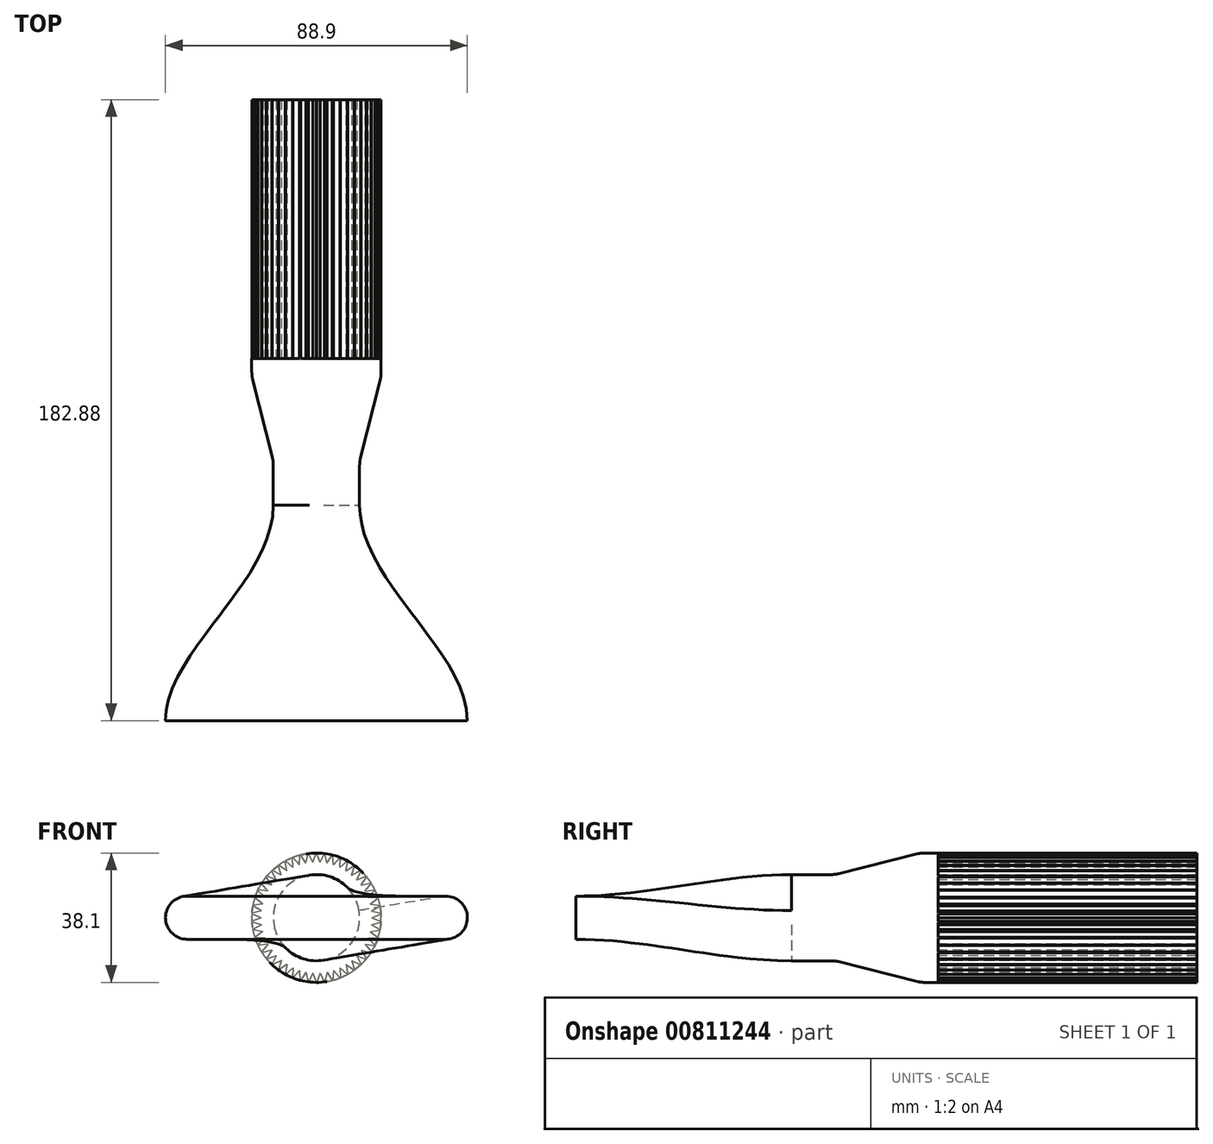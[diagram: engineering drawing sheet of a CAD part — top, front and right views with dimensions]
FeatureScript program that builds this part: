
annotation { "Feature Type Name" : "Feature", "Feature Type Description" : "" }
export const myFeature = defineFeature(function(context is Context, id is Id, definition is map)
    precondition{}
    {
        {
            var Q0;
            Q0=qCreatedBy(makeId("Front.planeOp"),FACE);
            var sketch = newSketch(context, id + "F0", { "sketchPlane" : qUnion([Q0])});
            skLineSegment(sketch, "E0.bottom", {"start": v(38.1, 6.35) * mm, "end": v(-38.1, 6.35) * mm});
            skLineSegment(sketch, "E0.top", {"start": v(38.1, -6.35) * mm, "end": v(-38.1, -6.35) * mm});
            skLineSegment(sketch, "E0.left", {"start": v(38.1, 6.35) * mm, "end": v(38.1, -6.35) * mm});
            skLineSegment(sketch, "E0.right", {"start": v(-38.1, 6.35) * mm, "end": v(-38.1, -6.35) * mm});
            skPoint(sketch, "E0.middle", {"position": v(0, 0) * mm});
            skArc(sketch, "E1", {"start": v(-38.1, 6.35) * mm, "mid": v(-44.45, 0) * mm, "end": v(-38.1, -6.35) * mm});
            skArc(sketch, "E2", {"start": v(38.1, -6.35) * mm, "mid": v(44.45, 0) * mm, "end": v(38.1, 6.35) * mm});
            skSolve(sketch);
        }
        {
            var Q0;
            Q0=qCreatedBy(makeId("Front.planeOp"),FACE);
            cPlane(context, id + "F1", {"entities" : qUnion([Q0]), "cplaneType" : CPlaneType.OFFSET, "offset" : 63.5 * mm, "oppositeDirection" : true, "width" : 152.4 * mm, "height" : 152.4 * mm});
        }
        {
            var Q0;
            Q0=qCreatedBy(id+"F1.planeOp",FACE);
            var sketch = newSketch(context, id + "F2", { "sketchPlane" : qUnion([Q0])});
            skCircle(sketch, "E3", {"center": v(0, 0) * mm, "radius": 12.7 * mm});
            skSolve(sketch);
        }
        {
            var Q0;
            Q0 = qSketchRegion(id + "F0", true);
            var Q1;
            Q1 = qSketchRegion(id + "F2", true);
            loft(context, id + "F3", {"startCondition" : LoftEndDerivativeType.NORMAL_TO_PROFILE, "startMagnitude" : 1, "endCondition" : LoftEndDerivativeType.NORMAL_TO_PROFILE, "endMagnitude" : 1, "sheetProfilesArray" : [{ "sheetProfileEntities" : qUnion([Q0]) }, { "sheetProfileEntities" : qUnion([Q1]) }]});
        }
        {
            var Q0;
            Q0=makeQuery(id+"F3.opLoft","CAP_FACE",FACE,{"disambiguationData":[OSD([makeQuery(id+"F2.imprint","IMPRINT",FACE,{"disambiguationData":[TD([[makeQuery(id+"F2.imprint","IMPRINT",EDGE,{"derivedFrom":sQuery(id+"F2.wireOp",EDGE,"E3")}),1.0]])]})])],"isStart":true});
            extrude(context, id + "F4", {"entities" : qUnion([Q0]), "operationType" : NewBodyOperationType.ADD, "depth" : 12.7 * mm, "offsetDistance" : 25.4 * mm});
        }
        {
            var Q0;
            Q0=makeQuery(id+"F4.opExtrude","CAP_FACE",FACE,{"disambiguationData":[OSD([makeQuery(id+"F2.imprint","IMPRINT",FACE,{"disambiguationData":[TD([[makeQuery(id+"F2.imprint","IMPRINT",EDGE,{"derivedFrom":sQuery(id+"F2.wireOp",EDGE,"E3")}),1.0]])]})])],"isStart":false});
            cPlane(context, id + "F5", {"entities" : qUnion([Q0]), "cplaneType" : CPlaneType.OFFSET, "offset" : 25.4 * mm, "width" : 152.4 * mm, "height" : 152.4 * mm});
        }
        {
            var Q0;
            Q0=qCreatedBy(id+"F5.planeOp",FACE);
            var sketch = newSketch(context, id + "F6", { "sketchPlane" : qUnion([Q0])});
            skCircle(sketch, "E4", {"center": v(0, 0) * mm, "radius": 19.05 * mm});
            skSolve(sketch);
        }
        {
            var Q1;
            Q1=makeQuery(id+"F6.imprint","IMPRINT",FACE,{"disambiguationData":[TD([[makeQuery(id+"F6.imprint","IMPRINT",EDGE,{"derivedFrom":sQuery(id+"F6.wireOp",EDGE,"E4")}),1.0]])]});
            var Q2;
            Q2=makeQuery(id+"F4.opExtrude","CAP_FACE",FACE,{"disambiguationData":[OSD([makeQuery(id+"F2.imprint","IMPRINT",FACE,{"disambiguationData":[TD([[makeQuery(id+"F2.imprint","IMPRINT",EDGE,{"derivedFrom":sQuery(id+"F2.wireOp",EDGE,"E3")}),1.0]])]})])],"isStart":false});
            loft(context, id + "F7", {"operationType" : NewBodyOperationType.ADD, "sheetProfilesArray" : [{ "sheetProfileEntities" : qUnion([Q1]) }, { "sheetProfileEntities" : qUnion([Q2]) }]});
        }
        {
            var Q0;
            Q0=makeQuery(id+"F7.opLoft","CAP_FACE",FACE,{"disambiguationData":[OSD([makeQuery(id+"F6.imprint","IMPRINT",FACE,{"disambiguationData":[TD([[makeQuery(id+"F6.imprint","IMPRINT",EDGE,{"derivedFrom":sQuery(id+"F6.wireOp",EDGE,"E4")}),1.0]])]})])],"isStart":true});
            extrude(context, id + "F8", {"entities" : qUnion([Q0]), "operationType" : NewBodyOperationType.ADD, "depth" : 5.08 * mm, "offsetDistance" : 25.4 * mm});
        }
        {
            var Q0;
            Q0=makeQuery(id+"F8.opExtrude","CAP_FACE",FACE,{"disambiguationData":[OSD([makeQuery(id+"F6.imprint","IMPRINT",FACE,{"disambiguationData":[TD([[makeQuery(id+"F6.imprint","IMPRINT",EDGE,{"derivedFrom":sQuery(id+"F6.wireOp",EDGE,"E4")}),1.0]])]})])],"isStart":false});
            var sketch = newSketch(context, id + "F9", { "sketchPlane" : qUnion([Q0])});
            skLineSegment(sketch, "E5", {"start": v(-16.3, 0) * mm, "end": v(-19.02, 1.1) * mm});
            skLineSegment(sketch, "E6.MirrorCS", {"start": v(-16.3, 0) * mm, "end": v(-19.02, -1.1) * mm});
            skLineSegment(sketch, "E7.1.0", {"start": v(-16.18, -2.04) * mm, "end": v(-19, -1.3) * mm});
            skLineSegment(sketch, "E7.1.1", {"start": v(-16.18, -2.04) * mm, "end": v(-18.73, -3.47) * mm});
            skLineSegment(sketch, "E7.2.0", {"start": v(-15.8, -4.06) * mm, "end": v(-18.7, -3.67) * mm});
            skLineSegment(sketch, "E7.2.1", {"start": v(-15.8, -4.06) * mm, "end": v(-18.15, -5.8) * mm});
            skLineSegment(sketch, "E7.3.0", {"start": v(-15.16, -6) * mm, "end": v(-18.09, -5.98) * mm});
            skLineSegment(sketch, "E7.3.1", {"start": v(-15.16, -6) * mm, "end": v(-17.28, -8.02) * mm});
            skPoint(sketch, "E7.center", {"position": v(0, 0) * mm});
            skLineSegment(sketch, "E8.3.4.0", {"start": v(-14.3, -7.86) * mm, "end": v(-16.14, -10.13) * mm});
            skLineSegment(sketch, "E8.5.4.0", {"start": v(-14.3, -7.86) * mm, "end": v(-17.2, -8.2) * mm});
            skLineSegment(sketch, "E8.3.5.0", {"start": v(-13.2, -9.59) * mm, "end": v(-14.74, -12.07) * mm});
            skLineSegment(sketch, "E8.5.5.0", {"start": v(-13.2, -9.59) * mm, "end": v(-16.03, -10.29) * mm});
            skLineSegment(sketch, "E8.3.6.0", {"start": v(-11.89, -11.16) * mm, "end": v(-13.11, -13.82) * mm});
            skLineSegment(sketch, "E8.5.6.0", {"start": v(-11.89, -11.16) * mm, "end": v(-14.62, -12.22) * mm});
            skLineSegment(sketch, "E8.3.7.0", {"start": v(-10.4, -12.57) * mm, "end": v(-11.28, -15.35) * mm});
            skLineSegment(sketch, "E8.5.7.0", {"start": v(-10.4, -12.57) * mm, "end": v(-12.97, -13.95) * mm});
            skLineSegment(sketch, "E8.3.8.0", {"start": v(-8.74, -13.77) * mm, "end": v(-9.26, -16.65) * mm});
            skLineSegment(sketch, "E8.5.8.0", {"start": v(-8.74, -13.77) * mm, "end": v(-11.12, -15.47) * mm});
            skLineSegment(sketch, "E8.3.9.0", {"start": v(-6.94, -14.76) * mm, "end": v(-7.1, -17.68) * mm});
            skLineSegment(sketch, "E8.5.9.0", {"start": v(-6.94, -14.76) * mm, "end": v(-9.1, -16.74) * mm});
            skLineSegment(sketch, "E8.3.10.0", {"start": v(-5.04, -15.51) * mm, "end": v(-4.83, -18.43) * mm});
            skLineSegment(sketch, "E8.5.10.0", {"start": v(-5.04, -15.51) * mm, "end": v(-6.92, -17.75) * mm});
            skLineSegment(sketch, "E8.3.11.0", {"start": v(-3.06, -16.02) * mm, "end": v(-2.48, -18.89) * mm});
            skLineSegment(sketch, "E8.5.11.0", {"start": v(-3.06, -16.02) * mm, "end": v(-4.64, -18.48) * mm});
            skLineSegment(sketch, "E8.3.12.0", {"start": v(-1.02, -16.28) * mm, "end": v(-0.1, -19.05) * mm});
            skLineSegment(sketch, "E8.5.12.0", {"start": v(-1.02, -16.28) * mm, "end": v(-2.3, -18.91) * mm});
            skLineSegment(sketch, "E8.3.13.0", {"start": v(1.02, -16.28) * mm, "end": v(2.3, -18.91) * mm});
            skLineSegment(sketch, "E8.5.13.0", {"start": v(1.02, -16.28) * mm, "end": v(0.1, -19.05) * mm});
            skLineSegment(sketch, "E8.3.14.0", {"start": v(3.06, -16.02) * mm, "end": v(4.64, -18.48) * mm});
            skLineSegment(sketch, "E8.5.14.0", {"start": v(3.06, -16.02) * mm, "end": v(2.48, -18.89) * mm});
            skLineSegment(sketch, "E8.3.15.0", {"start": v(5.04, -15.51) * mm, "end": v(6.92, -17.75) * mm});
            skLineSegment(sketch, "E8.5.15.0", {"start": v(5.04, -15.51) * mm, "end": v(4.83, -18.43) * mm});
            skLineSegment(sketch, "E8.3.16.0", {"start": v(6.94, -14.76) * mm, "end": v(9.1, -16.74) * mm});
            skLineSegment(sketch, "E8.5.16.0", {"start": v(6.94, -14.76) * mm, "end": v(7.1, -17.68) * mm});
            skLineSegment(sketch, "E8.3.17.0", {"start": v(8.74, -13.77) * mm, "end": v(11.12, -15.47) * mm});
            skLineSegment(sketch, "E8.5.17.0", {"start": v(8.74, -13.77) * mm, "end": v(9.26, -16.65) * mm});
            skLineSegment(sketch, "E8.3.18.0", {"start": v(10.4, -12.57) * mm, "end": v(12.97, -13.95) * mm});
            skLineSegment(sketch, "E8.5.18.0", {"start": v(10.4, -12.57) * mm, "end": v(11.28, -15.35) * mm});
            skLineSegment(sketch, "E8.3.19.0", {"start": v(11.89, -11.16) * mm, "end": v(14.62, -12.22) * mm});
            skLineSegment(sketch, "E8.5.19.0", {"start": v(11.89, -11.16) * mm, "end": v(13.11, -13.82) * mm});
            skLineSegment(sketch, "E8.3.20.0", {"start": v(13.2, -9.59) * mm, "end": v(16.03, -10.29) * mm});
            skLineSegment(sketch, "E8.5.20.0", {"start": v(13.2, -9.59) * mm, "end": v(14.74, -12.07) * mm});
            skLineSegment(sketch, "E8.3.21.0", {"start": v(14.3, -7.86) * mm, "end": v(17.2, -8.2) * mm});
            skLineSegment(sketch, "E8.5.21.0", {"start": v(14.3, -7.86) * mm, "end": v(16.14, -10.13) * mm});
            skLineSegment(sketch, "E8.3.22.0", {"start": v(15.16, -6) * mm, "end": v(18.09, -5.98) * mm});
            skLineSegment(sketch, "E8.5.22.0", {"start": v(15.16, -6) * mm, "end": v(17.28, -8.02) * mm});
            skLineSegment(sketch, "E8.3.23.0", {"start": v(15.8, -4.06) * mm, "end": v(18.7, -3.67) * mm});
            skLineSegment(sketch, "E8.5.23.0", {"start": v(15.8, -4.06) * mm, "end": v(18.15, -5.8) * mm});
            skLineSegment(sketch, "E8.3.24.0", {"start": v(16.18, -2.04) * mm, "end": v(19, -1.3) * mm});
            skLineSegment(sketch, "E8.5.24.0", {"start": v(16.18, -2.04) * mm, "end": v(18.73, -3.47) * mm});
            skLineSegment(sketch, "E8.3.25.0", {"start": v(16.3, 0) * mm, "end": v(19.02, 1.1) * mm});
            skLineSegment(sketch, "E8.5.25.0", {"start": v(16.3, 0) * mm, "end": v(19.02, -1.1) * mm});
            skLineSegment(sketch, "E8.3.26.0", {"start": v(16.18, 2.04) * mm, "end": v(18.73, 3.47) * mm});
            skLineSegment(sketch, "E8.5.26.0", {"start": v(16.18, 2.04) * mm, "end": v(19, 1.3) * mm});
            skLineSegment(sketch, "E8.3.27.0", {"start": v(15.8, 4.06) * mm, "end": v(18.15, 5.8) * mm});
            skLineSegment(sketch, "E8.5.27.0", {"start": v(15.8, 4.06) * mm, "end": v(18.7, 3.67) * mm});
            skLineSegment(sketch, "E8.3.28.0", {"start": v(15.16, 6) * mm, "end": v(17.28, 8.02) * mm});
            skLineSegment(sketch, "E8.5.28.0", {"start": v(15.16, 6) * mm, "end": v(18.09, 5.98) * mm});
            skLineSegment(sketch, "E8.3.29.0", {"start": v(14.3, 7.86) * mm, "end": v(16.14, 10.13) * mm});
            skLineSegment(sketch, "E8.5.29.0", {"start": v(14.3, 7.86) * mm, "end": v(17.2, 8.2) * mm});
            skLineSegment(sketch, "E8.3.30.0", {"start": v(13.2, 9.59) * mm, "end": v(14.74, 12.07) * mm});
            skLineSegment(sketch, "E8.5.30.0", {"start": v(13.2, 9.59) * mm, "end": v(16.03, 10.29) * mm});
            skLineSegment(sketch, "E8.3.31.0", {"start": v(11.89, 11.16) * mm, "end": v(13.11, 13.82) * mm});
            skLineSegment(sketch, "E8.5.31.0", {"start": v(11.89, 11.16) * mm, "end": v(14.62, 12.22) * mm});
            skLineSegment(sketch, "E8.3.32.0", {"start": v(10.4, 12.57) * mm, "end": v(11.28, 15.35) * mm});
            skLineSegment(sketch, "E8.5.32.0", {"start": v(10.4, 12.57) * mm, "end": v(12.97, 13.95) * mm});
            skLineSegment(sketch, "E8.3.33.0", {"start": v(8.74, 13.77) * mm, "end": v(9.26, 16.65) * mm});
            skLineSegment(sketch, "E8.5.33.0", {"start": v(8.74, 13.77) * mm, "end": v(11.12, 15.47) * mm});
            skLineSegment(sketch, "E8.3.34.0", {"start": v(6.94, 14.76) * mm, "end": v(7.1, 17.68) * mm});
            skLineSegment(sketch, "E8.5.34.0", {"start": v(6.94, 14.76) * mm, "end": v(9.1, 16.74) * mm});
            skLineSegment(sketch, "E8.3.35.0", {"start": v(5.04, 15.51) * mm, "end": v(4.83, 18.43) * mm});
            skLineSegment(sketch, "E8.5.35.0", {"start": v(5.04, 15.51) * mm, "end": v(6.92, 17.75) * mm});
            skLineSegment(sketch, "E8.3.36.0", {"start": v(3.06, 16.02) * mm, "end": v(2.48, 18.89) * mm});
            skLineSegment(sketch, "E8.5.36.0", {"start": v(3.06, 16.02) * mm, "end": v(4.64, 18.48) * mm});
            skLineSegment(sketch, "E8.3.37.0", {"start": v(1.02, 16.28) * mm, "end": v(0.1, 19.05) * mm});
            skLineSegment(sketch, "E8.5.37.0", {"start": v(1.02, 16.28) * mm, "end": v(2.3, 18.91) * mm});
            skLineSegment(sketch, "E8.3.38.0", {"start": v(-1.02, 16.28) * mm, "end": v(-2.3, 18.91) * mm});
            skLineSegment(sketch, "E8.5.38.0", {"start": v(-1.02, 16.28) * mm, "end": v(-0.1, 19.05) * mm});
            skLineSegment(sketch, "E8.3.39.0", {"start": v(-3.06, 16.02) * mm, "end": v(-4.64, 18.48) * mm});
            skLineSegment(sketch, "E8.5.39.0", {"start": v(-3.06, 16.02) * mm, "end": v(-2.48, 18.89) * mm});
            skLineSegment(sketch, "E8.3.40.0", {"start": v(-5.04, 15.51) * mm, "end": v(-6.92, 17.75) * mm});
            skLineSegment(sketch, "E8.5.40.0", {"start": v(-5.04, 15.51) * mm, "end": v(-4.83, 18.43) * mm});
            skLineSegment(sketch, "E8.3.41.0", {"start": v(-6.94, 14.76) * mm, "end": v(-9.1, 16.74) * mm});
            skLineSegment(sketch, "E8.5.41.0", {"start": v(-6.94, 14.76) * mm, "end": v(-7.1, 17.68) * mm});
            skLineSegment(sketch, "E8.3.42.0", {"start": v(-8.74, 13.77) * mm, "end": v(-11.12, 15.47) * mm});
            skLineSegment(sketch, "E8.5.42.0", {"start": v(-8.74, 13.77) * mm, "end": v(-9.26, 16.65) * mm});
            skLineSegment(sketch, "E8.3.43.0", {"start": v(-10.4, 12.57) * mm, "end": v(-12.97, 13.95) * mm});
            skLineSegment(sketch, "E8.5.43.0", {"start": v(-10.4, 12.57) * mm, "end": v(-11.28, 15.35) * mm});
            skLineSegment(sketch, "E8.3.44.0", {"start": v(-11.89, 11.16) * mm, "end": v(-14.62, 12.22) * mm});
            skLineSegment(sketch, "E8.5.44.0", {"start": v(-11.89, 11.16) * mm, "end": v(-13.11, 13.82) * mm});
            skLineSegment(sketch, "E8.3.45.0", {"start": v(-13.2, 9.59) * mm, "end": v(-16.03, 10.29) * mm});
            skLineSegment(sketch, "E8.5.45.0", {"start": v(-13.2, 9.59) * mm, "end": v(-14.74, 12.07) * mm});
            skLineSegment(sketch, "E8.3.46.0", {"start": v(-14.3, 7.86) * mm, "end": v(-17.2, 8.2) * mm});
            skLineSegment(sketch, "E8.5.46.0", {"start": v(-14.3, 7.86) * mm, "end": v(-16.14, 10.13) * mm});
            skLineSegment(sketch, "E8.3.47.0", {"start": v(-15.16, 6) * mm, "end": v(-18.09, 5.98) * mm});
            skLineSegment(sketch, "E8.5.47.0", {"start": v(-15.16, 6) * mm, "end": v(-17.28, 8.02) * mm});
            skLineSegment(sketch, "E8.3.48.0", {"start": v(-15.8, 4.06) * mm, "end": v(-18.7, 3.67) * mm});
            skLineSegment(sketch, "E8.5.48.0", {"start": v(-15.8, 4.06) * mm, "end": v(-18.15, 5.8) * mm});
            skLineSegment(sketch, "E8.3.49.0", {"start": v(-16.18, 2.04) * mm, "end": v(-19, 1.3) * mm});
            skLineSegment(sketch, "E8.5.49.0", {"start": v(-16.18, 2.04) * mm, "end": v(-18.73, 3.47) * mm});
            skSolve(sketch);
        }
        {
            var Q0;
            {var subQ77=sQuery(id+"F9.wireOp",EDGE,"E5");Q0=makeQuery(id+"F9.imprint","IMPRINT",FACE,{"disambiguationData":[TD([[makeQuery(id+"F9.imprint","IMPRINT",EDGE,{"derivedFrom":subQ77}),-1.0]])]});}
            extrude(context, id + "F10", {"entities" : qUnion([Q0]), "operationType" : NewBodyOperationType.ADD, "depth" : 76.2 * mm, "offsetDistance" : 25.4 * mm});
        }
        {
            var Q0;
            {var subQ0=sQuery(id+"F6.wireOp",EDGE,"E4");var subQ1=sQuery(id+"F2.wireOp",EDGE,"E3");var subQ2=sQuery(id+"F0.wireOp",EDGE,"E1");var subQ3=sQuery(id+"F0.wireOp",EDGE,"E0.right");var subQ4=sQuery(id+"F0.wireOp",EDGE,"E0.top");var subQ5=sQuery(id+"F0.wireOp",EDGE,"E2");var subQ6=sQuery(id+"F0.wireOp",EDGE,"E0.left");var subQ7=sQuery(id+"F0.wireOp",EDGE,"E0.bottom");var subQ8=makeQuery(id+"F7.opLoft","MID_CAP_EDGE",EDGE,{"disambiguationData":[OSD([subQ7,subQ4,subQ6,subQ3,subQ2,subQ5,subQ1,subQ0]),TDD([makeQuery(id+"F4.opExtrude","CAP_VERTEX",VERTEX,{"disambiguationData":[OSD([subQ7,subQ6,subQ5,subQ1])],"isStart":false}),makeQuery(id+"F4.opExtrude","CAP_VERTEX",VERTEX,{"disambiguationData":[OSD([subQ4,subQ3,subQ2,subQ1])],"isStart":false}),makeQuery(id+"F6.imprint","IMPRINT",EDGE,{"derivedFrom":subQ0})])],"capPos":0.0});Q0=makeQuery(id+"F8.boolean.opBoolean","MERGE",EDGE,{"derivedFrom":[subQ8,makeQuery(id+"F8.opExtrude","CAP_EDGE",EDGE,{"disambiguationData":[OSD([subQ7,subQ4,subQ6,subQ3,subQ2,subQ5,subQ1,subQ0]),TDD([subQ8])],"isStart":true})]});}
            var Q1;
            {var subQ0=sQuery(id+"F6.wireOp",EDGE,"E4");var subQ1=sQuery(id+"F0.wireOp",EDGE,"E2");var subQ2=sQuery(id+"F0.wireOp",EDGE,"E0.left");var subQ3=sQuery(id+"F0.wireOp",EDGE,"E0.bottom");var subQ4=sQuery(id+"F2.wireOp",EDGE,"E3");var subQ5=sQuery(id+"F0.wireOp",EDGE,"E1");var subQ6=sQuery(id+"F0.wireOp",EDGE,"E0.right");var subQ7=sQuery(id+"F0.wireOp",EDGE,"E0.top");var subQ8=makeQuery(id+"F7.opLoft","MID_CAP_EDGE",EDGE,{"disambiguationData":[OSD([subQ3,subQ7,subQ2,subQ6,subQ5,subQ1,subQ4,subQ0]),TDD([makeQuery(id+"F4.opExtrude","CAP_VERTEX",VERTEX,{"disambiguationData":[OSD([subQ7,subQ6,subQ5,subQ4])],"isStart":false}),makeQuery(id+"F4.opExtrude","CAP_VERTEX",VERTEX,{"disambiguationData":[OSD([subQ3,subQ2,subQ1])],"isStart":false}),makeQuery(id+"F6.imprint","IMPRINT",EDGE,{"derivedFrom":subQ0})])],"capPos":0.0});Q1=makeQuery(id+"F8.boolean.opBoolean","MERGE",EDGE,{"derivedFrom":[subQ8,makeQuery(id+"F8.opExtrude","CAP_EDGE",EDGE,{"disambiguationData":[OSD([subQ3,subQ7,subQ2,subQ6,subQ5,subQ1,subQ4,subQ0]),TDD([subQ8])],"isStart":true})]});}
            var Q2;
            {var subQ0=sQuery(id+"F6.wireOp",EDGE,"E4");var subQ1=sQuery(id+"F0.wireOp",EDGE,"E2");var subQ2=sQuery(id+"F0.wireOp",EDGE,"E0.left");var subQ3=sQuery(id+"F0.wireOp",EDGE,"E0.bottom");var subQ4=sQuery(id+"F2.wireOp",EDGE,"E3");var subQ5=makeQuery(id+"F7.opLoft","MID_CAP_EDGE",EDGE,{"disambiguationData":[OSD([subQ3,subQ2,subQ1,subQ4,subQ0]),TDD([makeQuery(id+"F4.opExtrude","CAP_VERTEX",VERTEX,{"disambiguationData":[OSD([subQ3,subQ2,subQ1,subQ4])],"isStart":false}),makeQuery(id+"F4.opExtrude","CAP_VERTEX",VERTEX,{"disambiguationData":[OSD([subQ3,subQ2,subQ1])],"isStart":false}),makeQuery(id+"F6.imprint","IMPRINT",EDGE,{"derivedFrom":subQ0})])],"capPos":0.0});Q2=makeQuery(id+"F8.boolean.opBoolean","MERGE",EDGE,{"derivedFrom":[subQ5,makeQuery(id+"F8.opExtrude","CAP_EDGE",EDGE,{"disambiguationData":[OSD([subQ3,subQ2,subQ1,subQ4,subQ0]),TDD([subQ5])],"isStart":true})]});}
            var Q3;
            {var subQ0=sQuery(id+"F6.wireOp",EDGE,"E4");var subQ1=sQuery(id+"F2.wireOp",EDGE,"E3");var subQ2=sQuery(id+"F0.wireOp",EDGE,"E2");var subQ3=sQuery(id+"F0.wireOp",EDGE,"E0.left");var subQ4=sQuery(id+"F0.wireOp",EDGE,"E0.bottom");var subQ5=makeQuery(id+"F7.opLoft","MID_CAP_EDGE",EDGE,{"disambiguationData":[OSD([subQ4,subQ3,subQ2,subQ1,subQ0]),TDD([makeQuery(id+"F4.opExtrude","CAP_VERTEX",VERTEX,{"disambiguationData":[OSD([subQ4,subQ3,subQ2,subQ1])],"isStart":false}),makeQuery(id+"F6.imprint","IMPRINT",EDGE,{"derivedFrom":subQ0})])],"capPos":0.0});Q3=makeQuery(id+"F8.boolean.opBoolean","MERGE",EDGE,{"derivedFrom":[subQ5,makeQuery(id+"F8.opExtrude","CAP_EDGE",EDGE,{"disambiguationData":[OSD([subQ4,subQ3,subQ2,subQ1,subQ0]),TDD([subQ5])],"isStart":true})]});}
            fillet(context, id + "F11", {"entities" : qUnion([Q0, Q1, Q2, Q3]), "radius" : 7.62 * mm, "tangentPropagation" : true, "allowEdgeOverflow" : false});
        }
        {
            var Q0;
            {var subQ0=sQuery(id+"F2.wireOp",EDGE,"E3");var subQ1=sQuery(id+"F0.wireOp",EDGE,"E2");var subQ2=sQuery(id+"F0.wireOp",EDGE,"E1");var subQ3=sQuery(id+"F0.wireOp",EDGE,"E0.right");var subQ4=sQuery(id+"F0.wireOp",EDGE,"E0.left");var subQ5=sQuery(id+"F0.wireOp",EDGE,"E0.top");var subQ6=sQuery(id+"F0.wireOp",EDGE,"E0.bottom");Q0=makeQuery(id+"F7.boolean.opBoolean","MERGE",EDGE,{"derivedFrom":[makeQuery(id+"F4.opExtrude","CAP_EDGE",EDGE,{"disambiguationData":[OSD([subQ6,subQ5,subQ4,subQ3,subQ2,subQ1,subQ0])],"isStart":false}),makeQuery(id+"F7.opLoft","MID_CAP_EDGE",EDGE,{"disambiguationData":[OSD([subQ6,subQ5,subQ4,subQ3,subQ2,subQ1,subQ0])],"capPos":1.0})]});}
            var Q1;
            {var subQ0=sQuery(id+"F2.wireOp",EDGE,"E3");var subQ1=sQuery(id+"F0.wireOp",EDGE,"E2");var subQ2=sQuery(id+"F0.wireOp",EDGE,"E0.left");var subQ3=sQuery(id+"F0.wireOp",EDGE,"E0.bottom");Q1=makeQuery(id+"F7.boolean.opBoolean","MERGE",EDGE,{"derivedFrom":[makeQuery(id+"F4.opExtrude","CAP_EDGE",EDGE,{"disambiguationData":[OSD([subQ3,subQ2,subQ1,subQ0])],"isStart":false}),makeQuery(id+"F7.opLoft","MID_CAP_EDGE",EDGE,{"disambiguationData":[OSD([subQ3,subQ2,subQ1,subQ0])],"capPos":1.0})]});}
            var Q2;
            {var subQ0=sQuery(id+"F2.wireOp",EDGE,"E3");var subQ1=sQuery(id+"F0.wireOp",EDGE,"E2");var subQ2=sQuery(id+"F0.wireOp",EDGE,"E1");var subQ3=sQuery(id+"F0.wireOp",EDGE,"E0.right");var subQ4=sQuery(id+"F0.wireOp",EDGE,"E0.left");var subQ5=sQuery(id+"F0.wireOp",EDGE,"E0.top");Q2=makeQuery(id+"F7.boolean.opBoolean","MERGE",EDGE,{"derivedFrom":[makeQuery(id+"F4.opExtrude","CAP_EDGE",EDGE,{"disambiguationData":[OSD([subQ5,subQ4,subQ3,subQ2,subQ1,subQ0])],"isStart":false}),makeQuery(id+"F7.opLoft","MID_CAP_EDGE",EDGE,{"disambiguationData":[OSD([subQ5,subQ4,subQ3,subQ2,subQ1,subQ0])],"capPos":1.0})]});}
            var Q3;
            {var subQ0=sQuery(id+"F2.wireOp",EDGE,"E3");var subQ1=sQuery(id+"F0.wireOp",EDGE,"E2");var subQ2=sQuery(id+"F0.wireOp",EDGE,"E0.left");var subQ3=sQuery(id+"F0.wireOp",EDGE,"E0.top");var subQ4=sQuery(id+"F0.wireOp",EDGE,"E0.bottom");Q3=makeQuery(id+"F7.boolean.opBoolean","MERGE",EDGE,{"derivedFrom":[makeQuery(id+"F4.opExtrude","CAP_EDGE",EDGE,{"disambiguationData":[OSD([subQ4,subQ3,subQ2,subQ1,subQ0])],"isStart":false}),makeQuery(id+"F7.opLoft","MID_CAP_EDGE",EDGE,{"disambiguationData":[OSD([subQ4,subQ3,subQ2,subQ1,subQ0])],"capPos":1.0})]});}
            fillet(context, id + "F12", {"entities" : qUnion([Q0, Q1, Q2, Q3]), "radius" : 7.62 * mm, "tangentPropagation" : true, "allowEdgeOverflow" : false});
        }
    });
